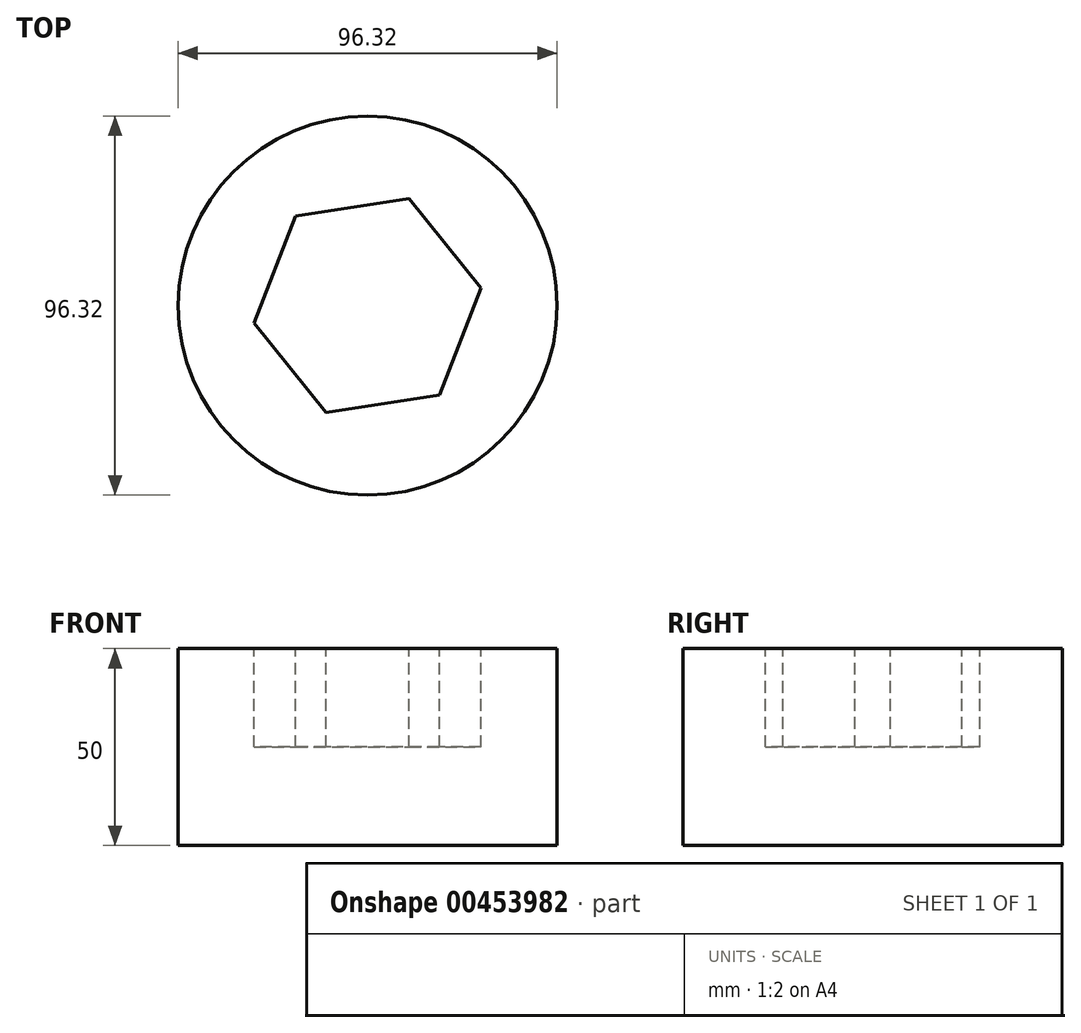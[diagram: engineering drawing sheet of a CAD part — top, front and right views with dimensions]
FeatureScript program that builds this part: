
annotation { "Feature Type Name" : "Feature", "Feature Type Description" : "" }
export const myFeature = defineFeature(function(context is Context, id is Id, definition is map)
    precondition{}
    {
        {
            var Q0;
            Q0=qCreatedBy(makeId("Top.planeOp"),FACE);
            var sketch = newSketch(context, id + "F0", { "sketchPlane" : qUnion([Q0])});
            skCircle(sketch, "E0", {"center": v(0, 0) * mm, "radius": 48.16 * mm});
            skSolve(sketch);
        }
        {
            var Q0;
            Q0=makeQuery(id+"F0.imprint","IMPRINT",FACE,{"disambiguationData":[TD([[makeQuery(id+"F0.imprint","IMPRINT",EDGE,{"derivedFrom":sQuery(id+"F0.wireOp",EDGE,"E0")}),1.0]])]});
            extrude(context, id + "F1", {"entities" : qUnion([Q0]), "depth" : 50 * mm});
        }
        {
            var Q0;
            Q0=makeQuery(id+"F1.opExtrude","CAP_FACE",FACE,{"disambiguationData":[OSD([sQuery(id+"F0.wireOp",EDGE,"E0")])],"isStart":false});
            var sketch = newSketch(context, id + "F2", { "sketchPlane" : qUnion([Q0])});
            skCircle(sketch, "E1.cCircle", {"center": v(0, 0) * mm, "radius": 25.26 * mm, "construction": true});
            skLineSegment(sketch, "E1.0", {"start": v(18.27, -22.74) * mm, "end": v(-10.55, -27.2) * mm});
            skLineSegment(sketch, "E1.1", {"start": v(-10.55, -27.2) * mm, "end": v(-28.83, -4.46) * mm});
            skLineSegment(sketch, "E1.2", {"start": v(-28.83, -4.46) * mm, "end": v(-18.27, 22.74) * mm});
            skLineSegment(sketch, "E1.3", {"start": v(-18.27, 22.74) * mm, "end": v(10.55, 27.2) * mm});
            skLineSegment(sketch, "E1.4", {"start": v(10.55, 27.2) * mm, "end": v(28.83, 4.46) * mm});
            skLineSegment(sketch, "E1.5", {"start": v(28.83, 4.46) * mm, "end": v(18.27, -22.74) * mm});
            skPoint(sketch, "E1.0.midPoint", {"position": v(3.86, -24.96) * mm});
            skSolve(sketch);
        }
        {
            var Q0;
            Q0 = qSketchRegion(id + "F2", true);
            extrude(context, id + "F3", {"entities" : qUnion([Q0]), "operationType" : NewBodyOperationType.REMOVE, "oppositeDirection" : true, "depth" : 25 * mm});
        }
    });
